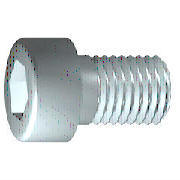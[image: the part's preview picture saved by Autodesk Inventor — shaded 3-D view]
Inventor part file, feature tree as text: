
AUTODESK INVENTOR PART (.ipt)
format: ipt  version: 2023.3 (Build 273359000, 359)  size: 189,952 bytes
history: native  units: mm (DEFAULTED — no unit token found)
features: sketch x2, other x1, extrude x1, plane x1, fillet x1
ambient origin geometry x7: Origin, YZ Plane, XY Plane, X Axis, Y Axis, Z Axis, Center Point
bodies: Solid1 (feature_tree)
feature tree (6):
  other  "Körper"
  extrude  "Loch"  Depth=2.5mm
  plane  "Work Plane1"
  fillet  "Fillet2"  Radius=2.5mm
  sketch  "Skizze1"  dims[d1=10.875mm d2=0.276153mm d3=2.5mm]
  sketch  "Skizze2"  dims[d4=1.1mm d5=60.0deg d6=2.5mm d7=2.5mm d8=2.309401mm d9=4.5mm d10=90.0deg d11=10.0mm d12=0.0mm d13=10.875mm d14=0.0mm d15=0.276052mm d16=0.276053mm d17=0.25mm d19=0.0mm d26=12.0mm d27=45.0deg d28=0.0mm d29=0.0mm d30=0.1mm]
